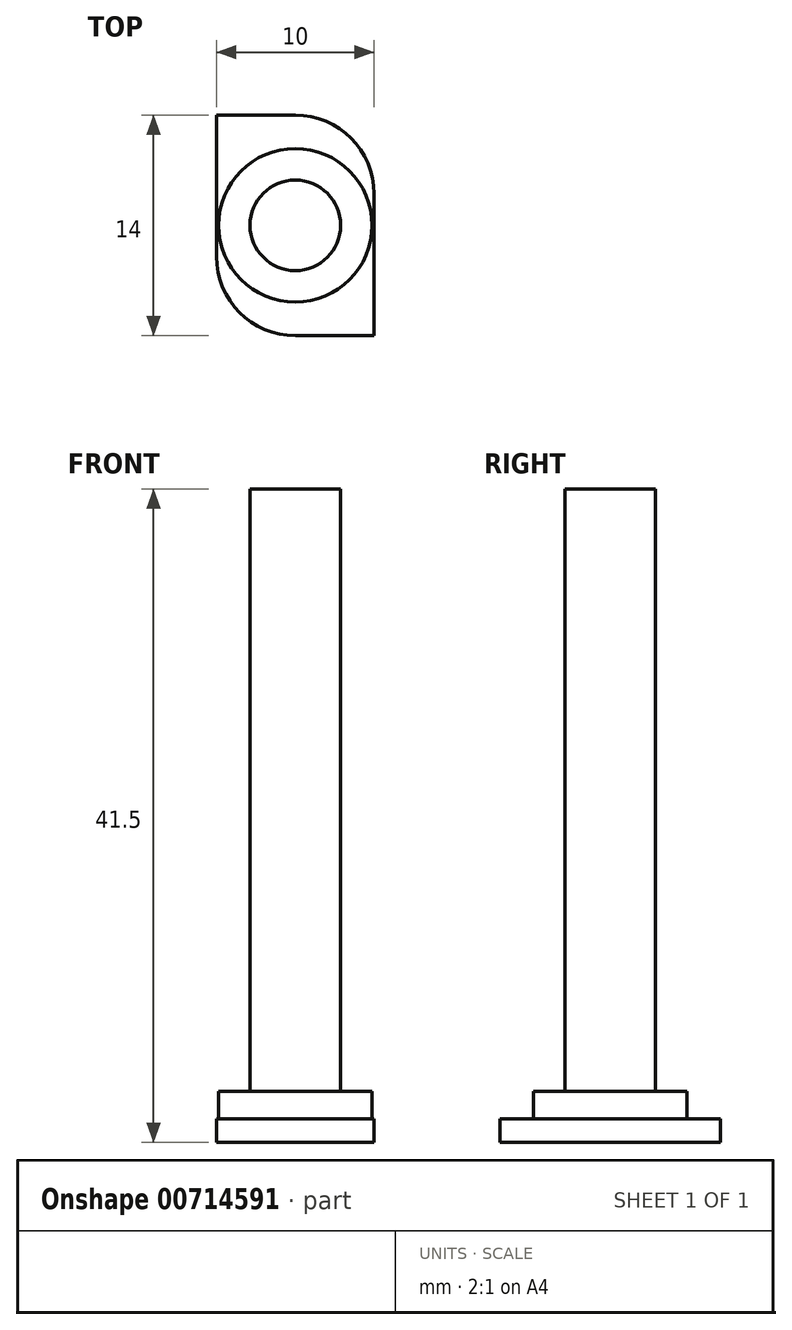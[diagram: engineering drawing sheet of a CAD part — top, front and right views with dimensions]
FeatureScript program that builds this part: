
annotation { "Feature Type Name" : "Feature", "Feature Type Description" : "" }
export const myFeature = defineFeature(function(context is Context, id is Id, definition is map)
    precondition{}
    {
        {
            var Q0;
            Q0=qCreatedBy(makeId("Top.planeOp"),FACE);
            var sketch = newSketch(context, id + "F0", { "sketchPlane" : qUnion([Q0])});
            skCircle(sketch, "E0", {"center": v(0, 0) * mm, "radius": 2.88 * mm});
            skSolve(sketch);
        }
        {
            var Q0;
            Q0=makeQuery(id+"F0.imprint","IMPRINT",FACE,{"disambiguationData":[TD([[makeQuery(id+"F0.imprint","IMPRINT",EDGE,{"derivedFrom":sQuery(id+"F0.wireOp",EDGE,"E0")}),1.0]])]});
            extrude(context, id + "F1", {"entities" : qUnion([Q0]), "endBound" : BoundingType.SYMMETRIC, "depth" : 40 * mm, "offsetDistance" : 25 * mm});
        }
        {
            var Q0;
            Q0=makeQuery(id+"F1.opExtrude","CAP_FACE",FACE,{"disambiguationData":[OSD([sQuery(id+"F0.wireOp",EDGE,"E0")])],"isStart":true});
            var sketch = newSketch(context, id + "F2", { "sketchPlane" : qUnion([Q0])});
            skLineSegment(sketch, "E1.bottom", {"start": v(-5, 7) * mm, "end": v(5, 7) * mm});
            skLineSegment(sketch, "E1.top", {"start": v(-5, -7) * mm, "end": v(5, -7) * mm});
            skLineSegment(sketch, "E1.left", {"start": v(-5, 7) * mm, "end": v(-5, -7) * mm});
            skLineSegment(sketch, "E1.right", {"start": v(5, 7) * mm, "end": v(5, -7) * mm});
            skPoint(sketch, "E1.middle", {"position": v(0, 0) * mm});
            skSolve(sketch);
        }
        {
            var Q0;
            Q0=makeQuery(id+"F2.imprint","IMPRINT",FACE,{"disambiguationData":[TD([[makeQuery(id+"F2.imprint","IMPRINT",EDGE,{"derivedFrom":sQuery(id+"F2.wireOp",EDGE,"E1.bottom")}),-1.0]])]});
            var Q1;
            Q1=makeQuery(id+"F2.imprint","IMPRINT",FACE,{"disambiguationData":[TD([[makeQuery(id+"F2.imprint","IMPRINT",EDGE,{"derivedFrom":makeQuery(id+"F1.opExtrude","CAP_EDGE",EDGE,{"disambiguationData":[OSD([sQuery(id+"F0.wireOp",EDGE,"E0")])],"isStart":true})}),-1.0]])]});
            extrude(context, id + "F3", {"entities" : qUnion([Q0, Q1]), "operationType" : NewBodyOperationType.ADD, "depth" : 1.5 * mm, "offsetDistance" : 25 * mm});
        }
        {
            var Q0;
            Q0=makeQuery(id+"F3.opExtrude","SWEPT_EDGE",EDGE,{"disambiguationData":[OSD([sQuery(id+"F2.wireOp",EDGE,"E1.bottom"),sQuery(id+"F2.wireOp",EDGE,"E1.left")])]});
            var Q1;
            Q1=makeQuery(id+"F3.opExtrude","SWEPT_EDGE",EDGE,{"disambiguationData":[OSD([sQuery(id+"F2.wireOp",EDGE,"E1.top"),sQuery(id+"F2.wireOp",EDGE,"E1.right")])]});
            fillet(context, id + "F4", {"entities" : qUnion([Q0, Q1]), "radius" : 5 * mm, "tangentPropagation" : true, "allowEdgeOverflow" : false});
        }
        {
            var Q0;
            Q0=makeQuery(id+"F3.opExtrude","CAP_FACE",FACE,{"disambiguationData":[OSD([sQuery(id+"F2.wireOp",EDGE,"E1.bottom"),sQuery(id+"F2.wireOp",EDGE,"E1.top"),sQuery(id+"F2.wireOp",EDGE,"E1.left"),sQuery(id+"F2.wireOp",EDGE,"E1.right")])],"isStart":true});
            var sketch = newSketch(context, id + "F5", { "sketchPlane" : qUnion([Q0])});
            skCircle(sketch, "E2.0", {"center": v(0, 0) * mm, "radius": 2.88 * mm});
            skCircle(sketch, "E3", {"center": v(0, 0) * mm, "radius": 4.88 * mm});
            skSolve(sketch);
        }
        {
            var Q0;
            Q0=makeQuery(id+"F5.imprint","IMPRINT",FACE,{"disambiguationData":[TD([[makeQuery(id+"F5.imprint","IMPRINT",EDGE,{"derivedFrom":sQuery(id+"F5.wireOp",EDGE,"E2.0")}),-1.0]])]});
            extrude(context, id + "F6", {"entities" : qUnion([Q0]), "operationType" : NewBodyOperationType.ADD, "depth" : 1.75 * mm, "offsetDistance" : 25 * mm});
        }
    });
